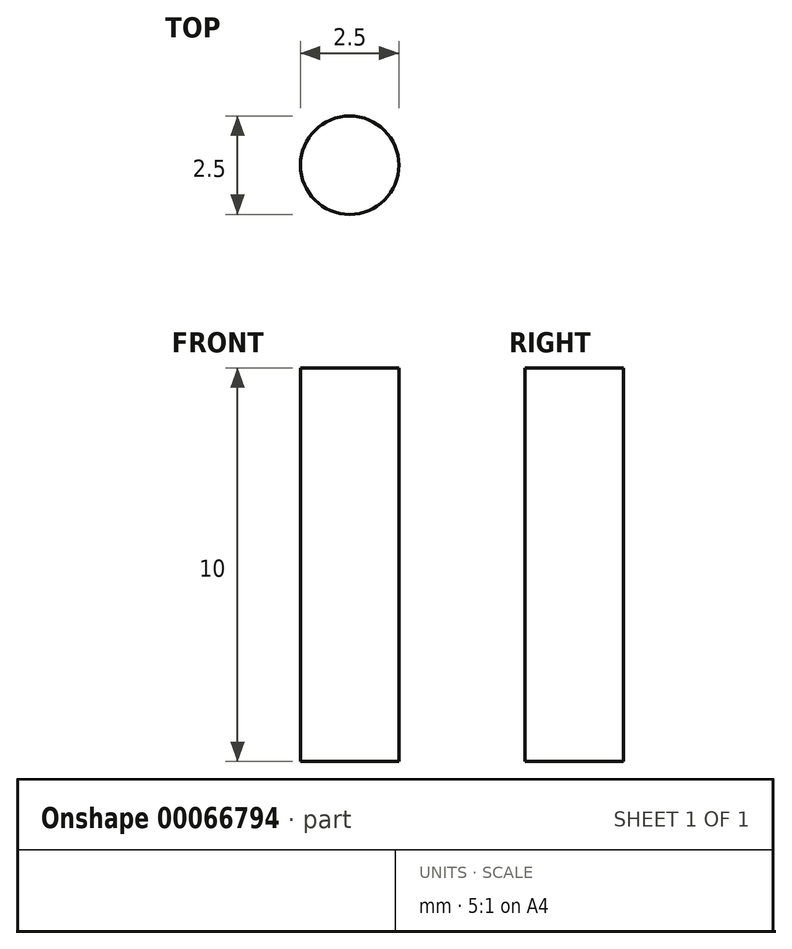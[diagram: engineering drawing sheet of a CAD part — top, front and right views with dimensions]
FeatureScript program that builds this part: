
annotation { "Feature Type Name" : "Feature", "Feature Type Description" : "" }
export const myFeature = defineFeature(function(context is Context, id is Id, definition is map)
    precondition{}
    {
        {
            var Q0;
            Q0=qCreatedBy(makeId("Top.planeOp"),FACE);
            var sketch = newSketch(context, id + "F0", { "sketchPlane" : qUnion([Q0])});
            skCircle(sketch, "E0", {"center": v(0, 0) * mm, "radius": 1.25 * mm});
            skSolve(sketch);
        }
        {
            var Q0;
            Q0=makeQuery(id+"F0.imprint","IMPRINT",FACE,{"disambiguationData":[TD([[makeQuery(id+"F0.imprint","IMPRINT",EDGE,{"derivedFrom":sQuery(id+"F0.wireOp",EDGE,"E0")}),1.0]])]});
            extrude(context, id + "F1", {"entities" : qUnion([Q0]), "endBound" : BoundingType.SYMMETRIC, "depth" : 10 * mm});
        }
    });
